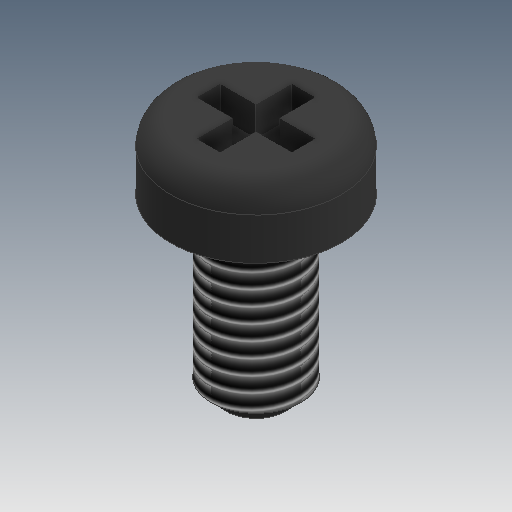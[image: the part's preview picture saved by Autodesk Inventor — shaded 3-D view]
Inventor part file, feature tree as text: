
AUTODESK INVENTOR PART (.ipt)
format: ipt  version: 2020 (Build 240168000, 168)  size: 173,056 bytes
history: native  units: mm
features: extrude x3, sketch x3, fillet x1, chamfer x1, thread x1
ambient origin geometry x8: Origin, YZ Plane, XZ Plane, XY Plane, X Axis, Y Axis, Z Axis, Center Point
bodies: Solid1 (feature_tree)
feature tree (9):
  extrude  "Extrusion1"  Depth=2.2mm TaperAngle=0.0deg
  extrude  "Extrusion2"  Depth=5.8mm TaperAngle=0.0deg
  fillet  "Fillet1"  Radius=0.8mm
  extrude  "Extrusion3"  Depth=0.8mm
  chamfer  "Chamfer1"  Distance=3.2mm
  thread  "Thread1"  [1 undecoded]
  sketch  "Sketch1"  dims[d0=5.7mm d1=2.2mm d2=0.0mm]
  sketch  "Sketch2"  dims[d3=3.0mm d4=5.8mm d5=0.0mm d6=0.8mm]
  sketch  "Sketch3"  dims[d7=0.8mm d8=0.8mm d9=3.2mm d10=3.2mm d11=1.0mm d12=0.0mm d13=0.5mm d14=2.0mm d15=45.0deg d16=5.3mm d17=0.0mm]
note: 1 required parameter value undecoded (feature->parameter linkage not recoverable at this tier; creation-order binding heuristic only, values carry confidence <= 0.55)
